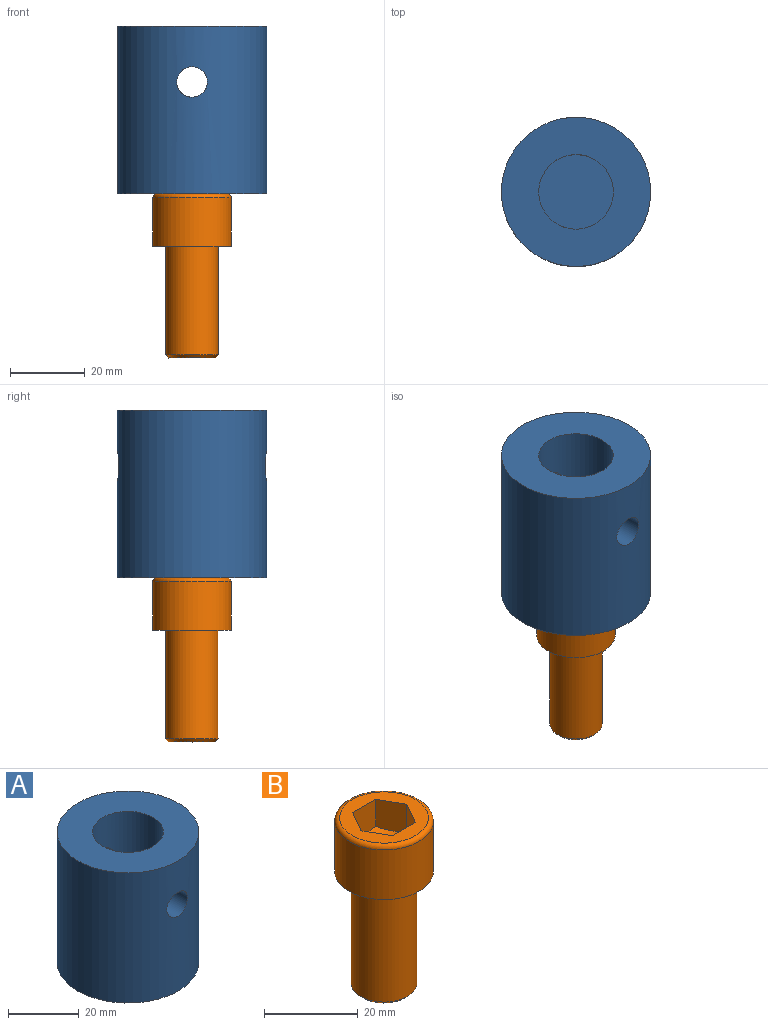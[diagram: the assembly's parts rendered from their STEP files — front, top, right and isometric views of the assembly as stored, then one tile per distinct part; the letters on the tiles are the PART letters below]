
ASSEMBLY  parts=2 mates=1
PART A: 7 faces, bbox 40x40x45 mm
  f0: cylinder r=20mm len=45mm, axis (0,0,-1), area 5548.9mm2, adj f2,f4,f5,f6
  f1: cylinder r=10mm len=28mm, axis (0,0,-1), area 1651.4mm2, adj f3,f4,f5,f6
  f2: plane 40x40mm, normal (0,0,-1), area 1256.6mm2, adj f0
  f3: plane 20x20mm, normal (0,0,1), area 314.2mm2, adj f1
  f4: plane 40x40mm, normal (0,0,1), area 942.5mm2, adj f0,f1
  f5: cylinder r=4.1mm len=10.88mm, axis (0,-1,0), area 263.4mm2, adj f0,f1
  f6: cylinder r=4.1mm len=10.88mm, axis (0,1,0), area 263.4mm2, adj f0,f1
PART B: 14 faces, bbox 22.7x22.7x44 mm
  f0: cylinder r=10.5mm len=21mm, axis (0,0,-1), area 854.4mm2, adj f1,f13
  f1: torus R=9.45mm, axis (0,0,-1), area 104.9mm2, adj f0,f12
  f2: cone r=6.59mm half-angle=45deg, axis (0,0,1), area 47.6mm2, adj f3,f11
  f3: cylinder r=7mm len=29.19mm, axis (0,0,-1), area 1283.8mm2, adj f2,f13
  f4: cone r=3.46mm half-angle=60deg, axis (0,0,1), area 144mm2, adj f5,f6,f7,f8,f9,f10
  f5: plane 7.79x6mm, normal (0.87,0.5,0), area 50.9mm2, adj f4,f6,f10,f12
  f6: plane 7.79x6.93mm, normal (0,1,0), area 50.9mm2, adj f4,f5,f7,f12
  f7: plane 7.79x6mm, normal (-0.87,0.5,0), area 50.9mm2, adj f4,f6,f8,f12
  f8: plane 7.79x6mm, normal (-0.87,-0.5,0), area 50.9mm2, adj f4,f7,f9,f12
  f9: plane 7.62x6.93mm, normal (0,-1,0), area 50.9mm2, adj f4,f8,f10,f12
  f10: plane 7.79x6mm, normal (0.87,-0.5,0), area 50.9mm2, adj f4,f5,f9,f12
  f11: plane 12.38x12.38mm, normal (0,0,-1), area 120.3mm2, adj f2
  f12: plane 18.9x18.9mm, normal (0,0,1), area 155.8mm2, adj f1,f5,f6,f7,f8,f9,f10
  f13: plane 21x21mm, normal (0,0,-1), area 192.4mm2, adj f0,f3
PLACE A t=(78.15,47.4,-16.78)mm
PLACE B t=(78.15,47.4,9.22)mm
MATE fastened A.f0 <-> B.f1  axis (0,0,-1) through (78.15,47.4,23.22)mm
